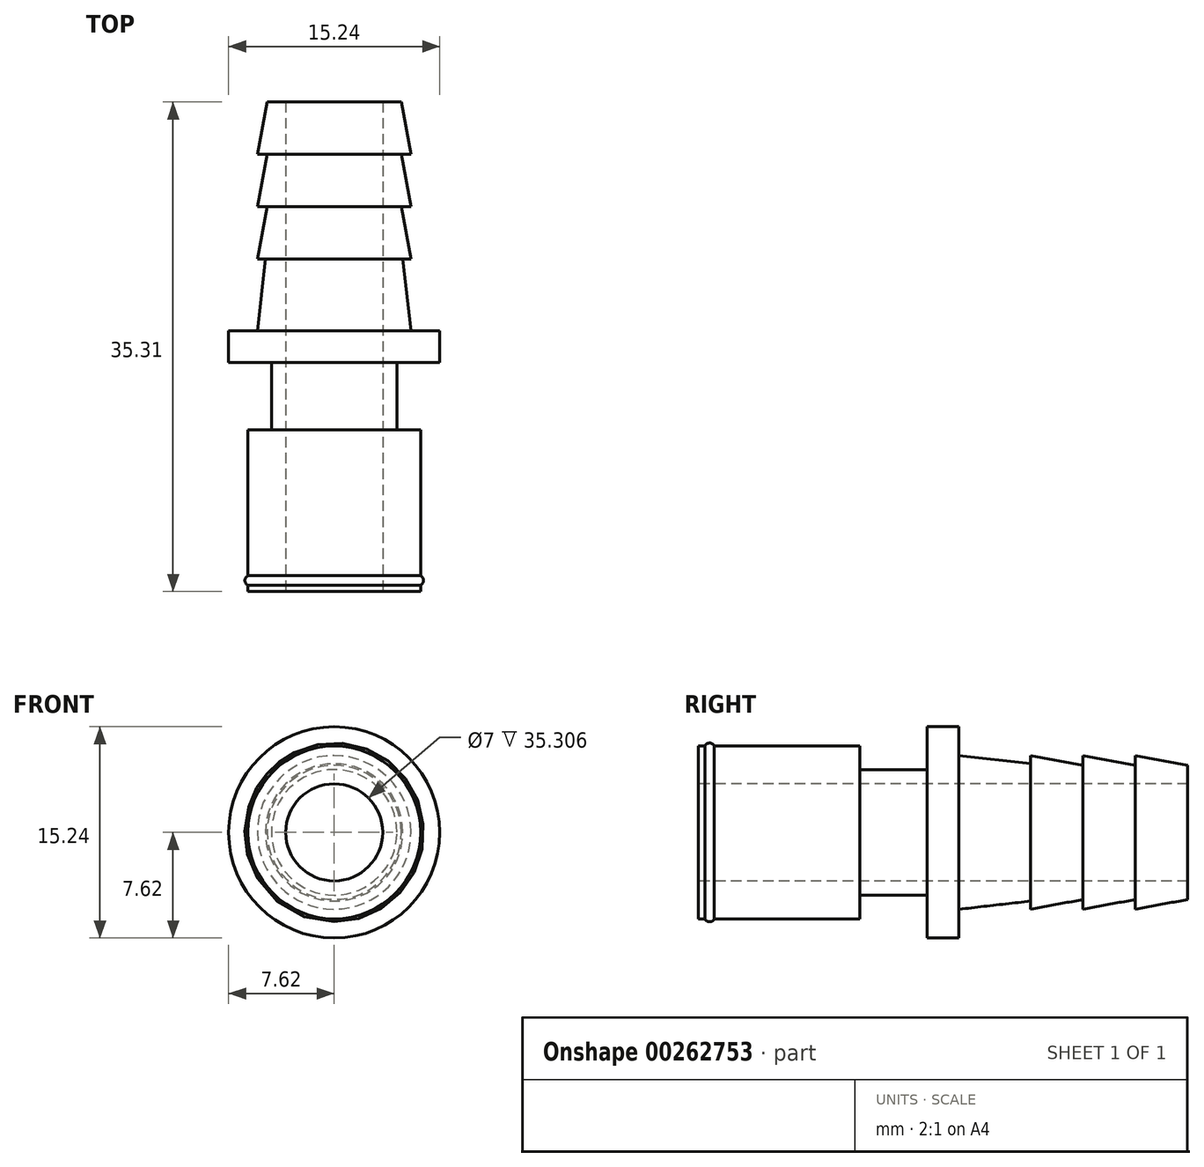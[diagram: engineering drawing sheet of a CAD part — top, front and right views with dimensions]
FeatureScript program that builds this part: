
annotation { "Feature Type Name" : "Feature", "Feature Type Description" : "" }
export const myFeature = defineFeature(function(context is Context, id is Id, definition is map)
    precondition{}
    {
        {
            var Q0;
            Q0=qCreatedBy(makeId("Right.planeOp"),FACE);
            var sketch = newSketch(context, id + "F0", { "sketchPlane" : qUnion([Q0])});
            skLineSegment(sketch, "E0", {"start": v(0, 6.23) * mm, "end": v(0.46, 6.23) * mm});
            skLineSegment(sketch, "E1", {"start": v(1.15, 6.23) * mm, "end": v(11.65, 6.23) * mm});
            skLineSegment(sketch, "E2", {"start": v(16.51, 4.53) * mm, "end": v(16.51, 7.62) * mm});
            skLineSegment(sketch, "E3", {"start": v(16.51, 7.62) * mm, "end": v(18.8, 7.62) * mm});
            skLineSegment(sketch, "E4", {"start": v(18.8, 7.62) * mm, "end": v(18.8, 5.54) * mm});
            skLineSegment(sketch, "E5", {"start": v(18.8, 5.54) * mm, "end": v(23.97, 4.95) * mm});
            skLineSegment(sketch, "E6", {"start": v(23.97, 4.95) * mm, "end": v(23.97, 5.54) * mm});
            skLineSegment(sketch, "E7", {"start": v(23.97, 5.54) * mm, "end": v(27.75, 4.84) * mm});
            skLineSegment(sketch, "E8", {"start": v(27.75, 4.84) * mm, "end": v(27.75, 5.54) * mm});
            skLineSegment(sketch, "E9", {"start": v(27.75, 5.54) * mm, "end": v(31.53, 4.84) * mm});
            skLineSegment(sketch, "E10", {"start": v(31.53, 4.84) * mm, "end": v(31.53, 5.54) * mm});
            skLineSegment(sketch, "E11", {"start": v(31.53, 5.54) * mm, "end": v(35.3, 4.84) * mm});
            skLineSegment(sketch, "E12", {"start": v(35.3, 4.84) * mm, "end": v(35.3, 3.5) * mm});
            skLineSegment(sketch, "E13", {"start": v(35.3, 3.5) * mm, "end": v(0, 3.5) * mm});
            skLineSegment(sketch, "E14", {"start": v(0, 3.5) * mm, "end": v(0, 6.23) * mm});
            skLineSegment(sketch, "E15", {"start": v(0, 0) * mm, "end": v(87.13, 0) * mm, "construction": true});
            skArc(sketch, "E16", {"start": v(1.15, 6.23) * mm, "mid": v(0.8, 6.45) * mm, "end": v(0.46, 6.23) * mm});
            skLineSegment(sketch, "E17", {"start": v(11.65, 6.23) * mm, "end": v(11.65, 4.53) * mm});
            skLineSegment(sketch, "E18", {"start": v(11.65, 4.53) * mm, "end": v(16.51, 4.53) * mm});
            skSolve(sketch);
        }
        {
            var Q0;
            Q0=makeQuery(id+"F0.imprint","IMPRINT",FACE,{"disambiguationData":[TD([[makeQuery(id+"F0.imprint","IMPRINT",EDGE,{"derivedFrom":sQuery(id+"F0.wireOp",EDGE,"E0")}),-1.0]])]});
            var Q1;
            Q1=sQuery(id+"F0.wireOp",EDGE,"E15");
            revolve(context, id + "F1", {"entities" : qUnion([Q0]), "axis" : qUnion([Q1]), "revolveType" : RevolveType.FULL});
        }
    });
